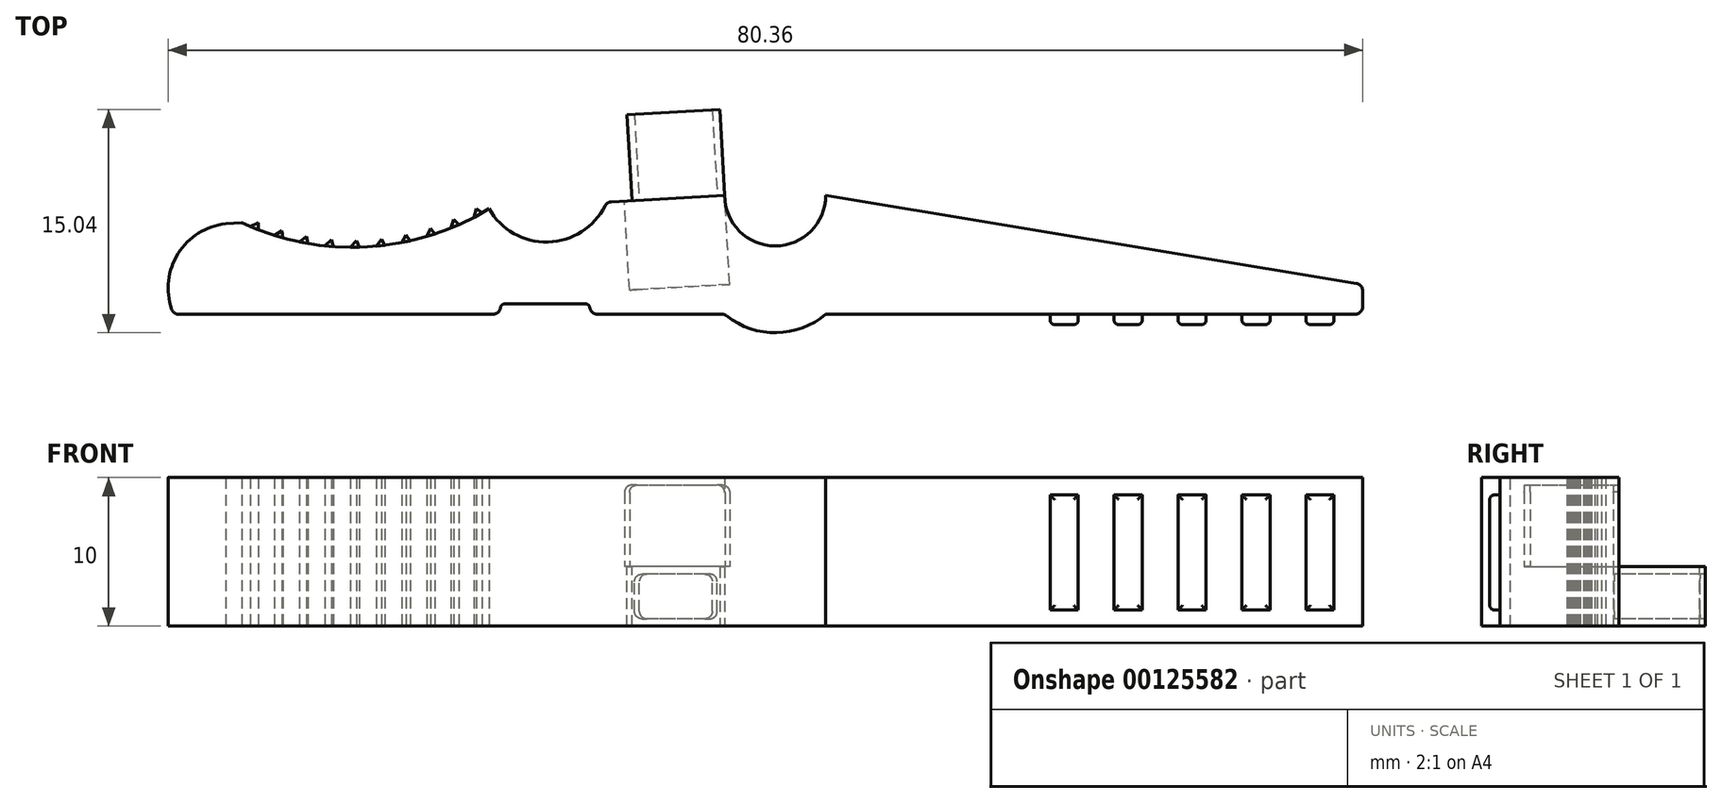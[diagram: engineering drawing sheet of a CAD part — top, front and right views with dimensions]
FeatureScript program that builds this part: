
annotation { "Feature Type Name" : "Feature", "Feature Type Description" : "" }
export const myFeature = defineFeature(function(context is Context, id is Id, definition is map)
    precondition{}
    {
        {
            var Q0;
            Q0=qCreatedBy(makeId("Top.planeOp"),FACE);
            var sketch = newSketch(context, id + "F0", { "sketchPlane" : qUnion([Q0])});
            skLineSegment(sketch, "E0", {"start": v(-43.88, 0) * mm, "end": v(-6.8, 0) * mm});
            skLineSegment(sketch, "E1", {"start": v(-6.8, 8) * mm, "end": v(-14.73, 7.55) * mm});
            skArc(sketch, "E2", {"start": v(-6.8, 8) * mm, "mid": v(-3.4, 4.6) * mm, "end": v(0, 8) * mm});
            skArc(sketch, "E3", {"start": v(-39.84, 6.13) * mm, "mid": v(-43.52, 4.16) * mm, "end": v(-43.88, 0) * mm});
            skArc(sketch, "E4", {"start": v(-39.28, 6.16) * mm, "mid": v(-30.85, 4.53) * mm, "end": v(-22.65, 7.1) * mm});
            skLineSegment(sketch, "E5.trimOffspring", {"start": v(-39.28, 6.16) * mm, "end": v(-40.38, 6.1) * mm});
            skArc(sketch, "E6", {"start": v(-22.65, 7.1) * mm, "mid": v(-18.55, 4.86) * mm, "end": v(-14.73, 7.55) * mm});
            skPoint(sketch, "E6.second.point", {"position": v(-14.73, 7.55) * mm});
            skLineSegment(sketch, "E7", {"start": v(0, 8) * mm, "end": v(36.12, 2) * mm});
            skLineSegment(sketch, "E8", {"start": v(36.12, 2) * mm, "end": v(36.12, 0) * mm});
            skLineSegment(sketch, "E9", {"start": v(-38.71, 5.9) * mm, "end": v(-38.17, 6.16) * mm});
            skLineSegment(sketch, "E10", {"start": v(-38.17, 6.16) * mm, "end": v(-38.17, 5.69) * mm});
            skLineSegment(sketch, "E11", {"start": v(-38.17, 5.69) * mm, "end": v(-38.71, 5.9) * mm});
            skLineSegment(sketch, "E12.1.0", {"start": v(-36.57, 5.61) * mm, "end": v(-36.53, 5.14) * mm});
            skLineSegment(sketch, "E12.1.1", {"start": v(-37.09, 5.3) * mm, "end": v(-36.57, 5.61) * mm});
            skLineSegment(sketch, "E12.1.2", {"start": v(-36.53, 5.14) * mm, "end": v(-37.09, 5.3) * mm});
            skLineSegment(sketch, "E12.2.0", {"start": v(-34.93, 5.23) * mm, "end": v(-34.84, 4.76) * mm});
            skLineSegment(sketch, "E12.2.1", {"start": v(-35.41, 4.87) * mm, "end": v(-34.93, 5.23) * mm});
            skLineSegment(sketch, "E12.2.2", {"start": v(-34.84, 4.76) * mm, "end": v(-35.41, 4.87) * mm});
            skLineSegment(sketch, "E12.3.0", {"start": v(-33.26, 5) * mm, "end": v(-33.12, 4.55) * mm});
            skLineSegment(sketch, "E12.3.1", {"start": v(-33.7, 4.6) * mm, "end": v(-33.26, 5) * mm});
            skLineSegment(sketch, "E12.3.2", {"start": v(-33.12, 4.55) * mm, "end": v(-33.7, 4.6) * mm});
            skLineSegment(sketch, "E12.4.0", {"start": v(-31.57, 4.94) * mm, "end": v(-31.39, 4.5) * mm});
            skLineSegment(sketch, "E12.4.1", {"start": v(-31.97, 4.5) * mm, "end": v(-31.57, 4.94) * mm});
            skLineSegment(sketch, "E12.4.2", {"start": v(-31.39, 4.5) * mm, "end": v(-31.97, 4.5) * mm});
            skLineSegment(sketch, "E12.5.0", {"start": v(-29.89, 5.05) * mm, "end": v(-29.66, 4.64) * mm});
            skLineSegment(sketch, "E12.5.1", {"start": v(-30.24, 4.57) * mm, "end": v(-29.89, 5.05) * mm});
            skLineSegment(sketch, "E12.5.2", {"start": v(-29.66, 4.64) * mm, "end": v(-30.24, 4.57) * mm});
            skLineSegment(sketch, "E12.6.0", {"start": v(-28.22, 5.33) * mm, "end": v(-27.96, 4.94) * mm});
            skLineSegment(sketch, "E12.6.1", {"start": v(-28.53, 4.82) * mm, "end": v(-28.22, 5.33) * mm});
            skLineSegment(sketch, "E12.6.2", {"start": v(-27.96, 4.94) * mm, "end": v(-28.53, 4.82) * mm});
            skLineSegment(sketch, "E12.7.0", {"start": v(-26.6, 5.77) * mm, "end": v(-26.29, 5.4) * mm});
            skLineSegment(sketch, "E12.7.1", {"start": v(-26.85, 5.23) * mm, "end": v(-26.6, 5.77) * mm});
            skLineSegment(sketch, "E12.7.2", {"start": v(-26.29, 5.4) * mm, "end": v(-26.85, 5.23) * mm});
            skLineSegment(sketch, "E12.8.0", {"start": v(-25.01, 6.37) * mm, "end": v(-24.67, 6.03) * mm});
            skLineSegment(sketch, "E12.8.1", {"start": v(-25.21, 5.8) * mm, "end": v(-25.01, 6.37) * mm});
            skLineSegment(sketch, "E12.8.2", {"start": v(-24.67, 6.03) * mm, "end": v(-25.21, 5.8) * mm});
            skLineSegment(sketch, "E12.9.0", {"start": v(-23.5, 7.12) * mm, "end": v(-23.13, 6.82) * mm});
            skLineSegment(sketch, "E12.9.1", {"start": v(-23.65, 6.53) * mm, "end": v(-23.5, 7.12) * mm});
            skLineSegment(sketch, "E12.9.2", {"start": v(-23.13, 6.82) * mm, "end": v(-23.65, 6.53) * mm});
            skLineSegment(sketch, "E12.anchor1", {"start": v(-31.84, 22) * mm, "end": v(-38.17, 5.69) * mm, "construction": true});
            skLineSegment(sketch, "E12.anchor2", {"start": v(-31.84, 22) * mm, "end": v(-23.13, 6.82) * mm, "construction": true});
            skLineSegment(sketch, "E13.bottom", {"start": v(-21.88, 0) * mm, "end": v(-15.88, 0) * mm});
            skLineSegment(sketch, "E13.top", {"start": v(-21.88, 0.7) * mm, "end": v(-15.88, 0.7) * mm});
            skLineSegment(sketch, "E13.left", {"start": v(-21.88, 0) * mm, "end": v(-21.88, 0.7) * mm});
            skLineSegment(sketch, "E13.right", {"start": v(-15.88, 0) * mm, "end": v(-15.88, 0.7) * mm});
            skArc(sketch, "E14", {"start": v(-6.8, 0) * mm, "mid": v(-3.4, -1.25) * mm, "end": v(0, 0) * mm});
            skPoint(sketch, "E14.first.point", {"position": v(-6.8, 0) * mm});
            skPoint(sketch, "E14.second.point", {"position": v(0, 0) * mm});
            skLineSegment(sketch, "E15.trimOffspring", {"start": v(0, 0) * mm, "end": v(36.12, 0) * mm});
            skSolve(sketch);
        }
        {
            var Q0;
            Q0=makeQuery(id+"F0.imprint","IMPRINT",FACE,{"disambiguationData":[TD([[makeQuery(id+"F0.imprint","IMPRINT",EDGE,{"derivedFrom":sQuery(id+"F0.wireOp",EDGE,"E12.1.0")}),-1.0]])]});
            var Q1;
            Q1=makeQuery(id+"F0.imprint","IMPRINT",FACE,{"disambiguationData":[TD([[makeQuery(id+"F0.imprint","IMPRINT",EDGE,{"derivedFrom":sQuery(id+"F0.wireOp",EDGE,"E9")}),-1.0]])]});
            var Q2;
            Q2=makeQuery(id+"F0.imprint","IMPRINT",FACE,{"disambiguationData":[TD([[makeQuery(id+"F0.imprint","IMPRINT",EDGE,{"derivedFrom":sQuery(id+"F0.wireOp",EDGE,"E12.2.0")}),-1.0]])]});
            var Q3;
            Q3=makeQuery(id+"F0.imprint","IMPRINT",FACE,{"disambiguationData":[TD([[makeQuery(id+"F0.imprint","IMPRINT",EDGE,{"derivedFrom":sQuery(id+"F0.wireOp",EDGE,"E12.3.0")}),-1.0]])]});
            var Q4;
            Q4=makeQuery(id+"F0.imprint","IMPRINT",FACE,{"disambiguationData":[TD([[makeQuery(id+"F0.imprint","IMPRINT",EDGE,{"derivedFrom":sQuery(id+"F0.wireOp",EDGE,"E12.4.0")}),-1.0]])]});
            var Q5;
            {var subQ22=sQuery(id+"F0.wireOp",EDGE,"E0");Q5=makeQuery(id+"F0.imprint","IMPRINT",FACE,{"disambiguationData":[TD([[makeQuery(id+"F0.imprint","IMPRINT",EDGE,{"derivedFrom":subQ22}),1.0]])]});}
            var Q6;
            Q6=makeQuery(id+"F0.imprint","IMPRINT",FACE,{"disambiguationData":[TD([[makeQuery(id+"F0.imprint","IMPRINT",EDGE,{"derivedFrom":sQuery(id+"F0.wireOp",EDGE,"E12.6.0")}),-1.0]])]});
            var Q7;
            Q7=makeQuery(id+"F0.imprint","IMPRINT",FACE,{"disambiguationData":[TD([[makeQuery(id+"F0.imprint","IMPRINT",EDGE,{"derivedFrom":sQuery(id+"F0.wireOp",EDGE,"E12.5.0")}),-1.0]])]});
            var Q8;
            Q8=makeQuery(id+"F0.imprint","IMPRINT",FACE,{"disambiguationData":[TD([[makeQuery(id+"F0.imprint","IMPRINT",EDGE,{"derivedFrom":sQuery(id+"F0.wireOp",EDGE,"E12.7.0")}),-1.0]])]});
            var Q9;
            Q9=makeQuery(id+"F0.imprint","IMPRINT",FACE,{"disambiguationData":[TD([[makeQuery(id+"F0.imprint","IMPRINT",EDGE,{"derivedFrom":sQuery(id+"F0.wireOp",EDGE,"E12.8.0")}),-1.0]])]});
            var Q10;
            Q10=makeQuery(id+"F0.imprint","IMPRINT",FACE,{"disambiguationData":[TD([[makeQuery(id+"F0.imprint","IMPRINT",EDGE,{"derivedFrom":sQuery(id+"F0.wireOp",EDGE,"E12.9.0")}),-1.0]])]});
            extrude(context, id + "F1", {"entities" : qUnion([Q0, Q1, Q2, Q3, Q4, Q5, Q6, Q7, Q8, Q9, Q10]), "depth" : 10 * mm});
        }
        {
            var Q0;
            Q0=makeQuery(id+"F1.opExtrude","SWEPT_EDGE",EDGE,{"disambiguationData":[OSD([sQuery(id+"F0.wireOp",EDGE,"E0"),sQuery(id+"F0.wireOp",EDGE,"E8")])]});
            var Q1;
            Q1=makeQuery(id+"F1.opExtrude","SWEPT_EDGE",EDGE,{"disambiguationData":[OSD([sQuery(id+"F0.wireOp",EDGE,"E7"),sQuery(id+"F0.wireOp",EDGE,"E8")])]});
            var Q2;
            Q2=makeQuery(id+"F1.opExtrude","SWEPT_EDGE",EDGE,{"disambiguationData":[OSD([sQuery(id+"F0.wireOp",EDGE,"E1"),sQuery(id+"F0.wireOp",EDGE,"E6")])]});
            var Q3;
            Q3=makeQuery(id+"F1.opExtrude","SWEPT_EDGE",EDGE,{"disambiguationData":[OSD([sQuery(id+"F0.wireOp",EDGE,"E0"),sQuery(id+"F0.wireOp",EDGE,"E3")])]});
            fillet(context, id + "F2", {"entities" : qUnion([Q0, Q1, Q2, Q3]), "radius" : 0.5 * mm, "tangentPropagation" : true, "allowEdgeOverflow" : false});
        }
        {
            var Q0;
            Q0=makeQuery(id+"F1.opExtrude","SWEPT_FACE",FACE,{"disambiguationData":[OSD([sQuery(id+"F0.wireOp",EDGE,"E1")])]});
            var sketch = newSketch(context, id + "F3", { "sketchPlane" : qUnion([Q0])});
            skLineSegment(sketch, "E16.bottom", {"start": v(6.34, 0) * mm, "end": v(12.59, 0) * mm});
            skLineSegment(sketch, "E16.top", {"start": v(6.34, 4) * mm, "end": v(12.59, 4) * mm});
            skLineSegment(sketch, "E16.left", {"start": v(6.34, 0) * mm, "end": v(6.34, 4) * mm});
            skLineSegment(sketch, "E16.right", {"start": v(12.59, 0) * mm, "end": v(12.59, 4) * mm});
            skLineSegment(sketch, "E17.0", {"start": v(6.84, 0.5) * mm, "end": v(12.09, 0.5) * mm});
            skLineSegment(sketch, "E17.1", {"start": v(6.84, 0.5) * mm, "end": v(6.84, 3.5) * mm});
            skLineSegment(sketch, "E17.2", {"start": v(6.84, 3.5) * mm, "end": v(12.09, 3.5) * mm});
            skLineSegment(sketch, "E17.3", {"start": v(12.09, 0.5) * mm, "end": v(12.09, 3.5) * mm});
            skSolve(sketch);
        }
        {
            var Q0;
            Q0 = qSketchRegion(id + "F3", true);
            extrude(context, id + "F4", {"entities" : qUnion([Q0]), "operationType" : NewBodyOperationType.ADD, "depth" : 5.8 * mm});
        }
        {
            var Q0;
            Q0=makeQuery(id+"F4.opExtrude","SWEPT_EDGE",EDGE,{"disambiguationData":[OSD([sQuery(id+"F3.wireOp",EDGE,"E17.0"),sQuery(id+"F3.wireOp",EDGE,"E17.3")])]});
            var Q1;
            Q1=makeQuery(id+"F4.opExtrude","SWEPT_EDGE",EDGE,{"disambiguationData":[OSD([sQuery(id+"F3.wireOp",EDGE,"E17.2"),sQuery(id+"F3.wireOp",EDGE,"E17.3")])]});
            var Q2;
            Q2=makeQuery(id+"F4.opExtrude","SWEPT_EDGE",EDGE,{"disambiguationData":[OSD([sQuery(id+"F3.wireOp",EDGE,"E17.1"),sQuery(id+"F3.wireOp",EDGE,"E17.2")])]});
            var Q3;
            Q3=makeQuery(id+"F4.opExtrude","SWEPT_EDGE",EDGE,{"disambiguationData":[OSD([sQuery(id+"F3.wireOp",EDGE,"E17.0"),sQuery(id+"F3.wireOp",EDGE,"E17.1")])]});
            fillet(context, id + "F5", {"entities" : qUnion([Q0, Q1, Q2, Q3]), "radius" : 0.5 * mm, "tangentPropagation" : true, "allowEdgeOverflow" : false});
        }
        {
            var Q0;
            Q0=makeQuery(id+"F1.opExtrude","SWEPT_FACE",FACE,{"disambiguationData":[OSD([sQuery(id+"F0.wireOp",EDGE,"E0")])]});
            var sketch = newSketch(context, id + "F6", { "sketchPlane" : qUnion([Q0])});
            skLineSegment(sketch, "E18.bottom", {"start": v(34.2, 1.1) * mm, "end": v(32.3, 1.1) * mm});
            skLineSegment(sketch, "E18.top", {"start": v(34.2, 8.83) * mm, "end": v(32.3, 8.83) * mm});
            skLineSegment(sketch, "E18.left", {"start": v(34.2, 1.1) * mm, "end": v(34.2, 8.83) * mm});
            skLineSegment(sketch, "E18.right", {"start": v(32.3, 1.1) * mm, "end": v(32.3, 8.83) * mm});
            skLineSegment(sketch, "E19.1.0.0", {"start": v(28, 1.1) * mm, "end": v(28, 8.83) * mm});
            skLineSegment(sketch, "E19.1.0.1", {"start": v(29.9, 1.1) * mm, "end": v(28, 1.1) * mm});
            skLineSegment(sketch, "E19.1.0.2", {"start": v(29.9, 1.1) * mm, "end": v(29.9, 8.83) * mm});
            skLineSegment(sketch, "E19.1.0.3", {"start": v(29.9, 8.83) * mm, "end": v(28, 8.83) * mm});
            skLineSegment(sketch, "E19.2.0.0", {"start": v(23.7, 1.1) * mm, "end": v(23.7, 8.83) * mm});
            skLineSegment(sketch, "E19.2.0.1", {"start": v(25.6, 1.1) * mm, "end": v(23.7, 1.1) * mm});
            skLineSegment(sketch, "E19.2.0.2", {"start": v(25.6, 1.1) * mm, "end": v(25.6, 8.83) * mm});
            skLineSegment(sketch, "E19.2.0.3", {"start": v(25.6, 8.83) * mm, "end": v(23.7, 8.83) * mm});
            skLineSegment(sketch, "E19.3.0.0", {"start": v(19.4, 1.1) * mm, "end": v(19.4, 8.83) * mm});
            skLineSegment(sketch, "E19.3.0.1", {"start": v(21.29, 1.1) * mm, "end": v(19.4, 1.1) * mm});
            skLineSegment(sketch, "E19.3.0.2", {"start": v(21.29, 1.1) * mm, "end": v(21.29, 8.83) * mm});
            skLineSegment(sketch, "E19.3.0.3", {"start": v(21.29, 8.83) * mm, "end": v(19.4, 8.83) * mm});
            skLineSegment(sketch, "E19.4.0.0", {"start": v(15.1, 1.1) * mm, "end": v(15.1, 8.83) * mm});
            skLineSegment(sketch, "E19.4.0.1", {"start": v(16.99, 1.1) * mm, "end": v(15.1, 1.1) * mm});
            skLineSegment(sketch, "E19.4.0.2", {"start": v(16.99, 1.1) * mm, "end": v(16.99, 8.83) * mm});
            skLineSegment(sketch, "E19.4.0.3", {"start": v(16.99, 8.83) * mm, "end": v(15.1, 8.83) * mm});
            skLineSegment(sketch, "E19.direction1", {"start": v(32.3, 1.1) * mm, "end": v(28, 1.1) * mm, "construction": true});
            skSolve(sketch);
        }
        {
            var Q0;
            Q0 = qSketchRegion(id + "F6", true);
            extrude(context, id + "F7", {"entities" : qUnion([Q0]), "operationType" : NewBodyOperationType.ADD, "depth" : 0.7 * mm});
        }
        {
            var Q0;
            Q0=makeQuery(id+"F7.opExtrude","CAP_FACE",FACE,{"disambiguationData":[OSD([sQuery(id+"F6.wireOp",EDGE,"E18.bottom"),sQuery(id+"F6.wireOp",EDGE,"E18.top"),sQuery(id+"F6.wireOp",EDGE,"E18.left"),sQuery(id+"F6.wireOp",EDGE,"E18.right")])],"isStart":false});
            var Q1;
            Q1=makeQuery(id+"F7.opExtrude","CAP_FACE",FACE,{"disambiguationData":[OSD([sQuery(id+"F6.wireOp",EDGE,"E19.1.0.0"),sQuery(id+"F6.wireOp",EDGE,"E19.1.0.1"),sQuery(id+"F6.wireOp",EDGE,"E19.1.0.2"),sQuery(id+"F6.wireOp",EDGE,"E19.1.0.3")])],"isStart":false});
            var Q2;
            Q2=makeQuery(id+"F7.opExtrude","CAP_FACE",FACE,{"disambiguationData":[OSD([sQuery(id+"F6.wireOp",EDGE,"E19.2.0.0"),sQuery(id+"F6.wireOp",EDGE,"E19.2.0.1"),sQuery(id+"F6.wireOp",EDGE,"E19.2.0.2"),sQuery(id+"F6.wireOp",EDGE,"E19.2.0.3")])],"isStart":false});
            var Q3;
            Q3=makeQuery(id+"F7.opExtrude","CAP_FACE",FACE,{"disambiguationData":[OSD([sQuery(id+"F6.wireOp",EDGE,"E19.3.0.0"),sQuery(id+"F6.wireOp",EDGE,"E19.3.0.1"),sQuery(id+"F6.wireOp",EDGE,"E19.3.0.2"),sQuery(id+"F6.wireOp",EDGE,"E19.3.0.3")])],"isStart":false});
            var Q4;
            Q4=makeQuery(id+"F7.opExtrude","CAP_FACE",FACE,{"disambiguationData":[OSD([sQuery(id+"F6.wireOp",EDGE,"E19.4.0.0"),sQuery(id+"F6.wireOp",EDGE,"E19.4.0.1"),sQuery(id+"F6.wireOp",EDGE,"E19.4.0.2"),sQuery(id+"F6.wireOp",EDGE,"E19.4.0.3")])],"isStart":false});
            fillet(context, id + "F8", {"entities" : qUnion([Q0, Q1, Q2, Q3, Q4]), "radius" : 0.3 * mm, "tangentPropagation" : true, "allowEdgeOverflow" : false});
        }
        {
            var Q0;
            Q0=makeQuery(id+"F1.opExtrude","SWEPT_EDGE",EDGE,{"disambiguationData":[OSD([sQuery(id+"F0.wireOp",EDGE,"E0"),sQuery(id+"F0.wireOp",EDGE,"E13.bottom"),sQuery(id+"F0.wireOp",EDGE,"E13.left")])]});
            var Q1;
            Q1=makeQuery(id+"F1.opExtrude","SWEPT_EDGE",EDGE,{"disambiguationData":[OSD([sQuery(id+"F0.wireOp",EDGE,"E0"),sQuery(id+"F0.wireOp",EDGE,"E13.bottom"),sQuery(id+"F0.wireOp",EDGE,"E13.right")])]});
            var Q2;
            Q2=makeQuery(id+"F1.opExtrude","SWEPT_EDGE",EDGE,{"disambiguationData":[OSD([sQuery(id+"F0.wireOp",EDGE,"E13.top"),sQuery(id+"F0.wireOp",EDGE,"E13.left")])]});
            var Q3;
            Q3=makeQuery(id+"F1.opExtrude","SWEPT_EDGE",EDGE,{"disambiguationData":[OSD([sQuery(id+"F0.wireOp",EDGE,"E13.top"),sQuery(id+"F0.wireOp",EDGE,"E13.right")])]});
            fillet(context, id + "F9", {"entities" : qUnion([Q0, Q1, Q2, Q3]), "radius" : 0.3 * mm, "tangentPropagation" : true, "allowEdgeOverflow" : false});
        }
        {
            var Q0;
            {var subQ1=sQuery(id+"F0.wireOp",EDGE,"E1");var subQ2=sQuery(id+"F0.wireOp",EDGE,"E2");Q0=makeQuery(id+"F4.boolean.opBoolean","SPLIT",FACE,{"disambiguationData":[TD([makeQuery(id+"F1.opExtrude","SWEPT_FACE",FACE,{"disambiguationData":[OSD([subQ2])]})])],"derivedFrom":makeQuery(id+"F1.opExtrude","SWEPT_FACE",FACE,{"disambiguationData":[OSD([subQ1])]})});}
            var sketch = newSketch(context, id + "F10", { "sketchPlane" : qUnion([Q0])});
            skLineSegment(sketch, "E20.bottom", {"start": v(6.34, 10) * mm, "end": v(13.09, 10) * mm});
            skLineSegment(sketch, "E20.top", {"start": v(6.34, 4) * mm, "end": v(13.09, 4) * mm});
            skLineSegment(sketch, "E20.left", {"start": v(6.34, 10) * mm, "end": v(6.34, 4) * mm});
            skLineSegment(sketch, "E20.right", {"start": v(13.09, 10) * mm, "end": v(13.09, 4) * mm});
            skLineSegment(sketch, "E21", {"start": v(13.09, 9.5) * mm, "end": v(6.34, 9.5) * mm});
            skSolve(sketch);
        }
        {
            var Q0;
            {var subQ3=sQuery(id+"F10.wireOp",EDGE,"E21");Q0=makeQuery(id+"F10.imprint","IMPRINT",FACE,{"disambiguationData":[TD([[makeQuery(id+"F10.imprint","IMPRINT",EDGE,{"derivedFrom":subQ3}),1.0]])]});}
            extrude(context, id + "F11", {"entities" : qUnion([Q0]), "operationType" : NewBodyOperationType.REMOVE, "oppositeDirection" : true, "depth" : 6 * mm});
        }
        {
            var Q0;
            Q0=makeQuery(id+"F11.boolean.opBoolean","COPY",EDGE,{"derivedFrom":makeQuery(id+"F11.opExtrude","SWEPT_EDGE",EDGE,{"disambiguationData":[OSD([sQuery(id+"F10.wireOp",EDGE,"E20.right"),sQuery(id+"F10.wireOp",EDGE,"E21")])]})});
            var Q1;
            Q1=makeQuery(id+"F11.boolean.opBoolean","COPY",EDGE,{"derivedFrom":makeQuery(id+"F11.opExtrude","SWEPT_EDGE",EDGE,{"disambiguationData":[OSD([sQuery(id+"F10.wireOp",EDGE,"E20.left"),sQuery(id+"F10.wireOp",EDGE,"E21")])]})});
            fillet(context, id + "F12", {"entities" : qUnion([Q0, Q1]), "radius" : 0.5 * mm, "tangentPropagation" : true, "allowEdgeOverflow" : false});
        }
    });
